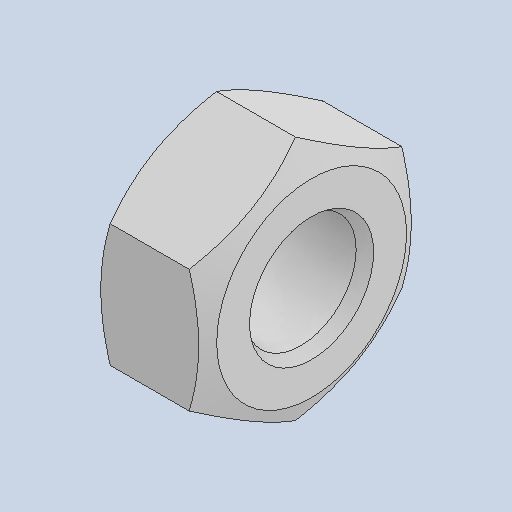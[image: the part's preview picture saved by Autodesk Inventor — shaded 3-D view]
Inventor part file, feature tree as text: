
AUTODESK INVENTOR PART (.ipt)
format: ipt  version: 2022 (Build 260153000, 153)  size: 115,200 bytes
history: native  units: in
note: dims shown in document units (in); Inventor stores cm internally (conversion verified against a paired STEP export)
features: chamfer x1
ambient origin geometry x8: Origin, YZ Plane, XZ Plane, XY Plane, X Axis, Y Axis, Z Axis, Center Point
bodies: Solid1 (feature_tree)
feature tree (1):
  chamfer  "Chamfer3"  [1 undecoded]
note: 1 required parameter value undecoded (feature->parameter linkage not recoverable at this tier; creation-order binding heuristic only, values carry confidence <= 0.55)
